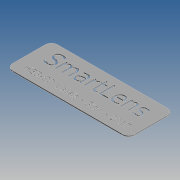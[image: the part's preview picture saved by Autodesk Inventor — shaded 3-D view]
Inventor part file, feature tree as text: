
AUTODESK INVENTOR PART (.ipt)
format: ipt  version: 2015 SP1 (Build 190203100, 203)  size: 830,976 bytes
history: native  units: mm
features: extrude x2, sketch x2, fillet x1
ambient origin geometry x8: Origin, YZ Plane, XZ Plane, XY Plane, X Axis, Y Axis, Z Axis, Center Point
bodies: Solid1 (feature_tree)
feature tree (5):
  extrude  "Extrusion1"  Depth=0.4mm
  fillet  "Fillet1"  Radius=0.4mm
  extrude  "Extrusion2"  Depth=0.4mm TaperAngle=0.0deg
  sketch  "Sketch1"  dims[d0=39.5mm d1=14.5mm d2=0.4mm d3=0.0mm]
  sketch  "Sketch2"  dims[d4=2.0mm d5=0.4mm d6=0.0mm]
